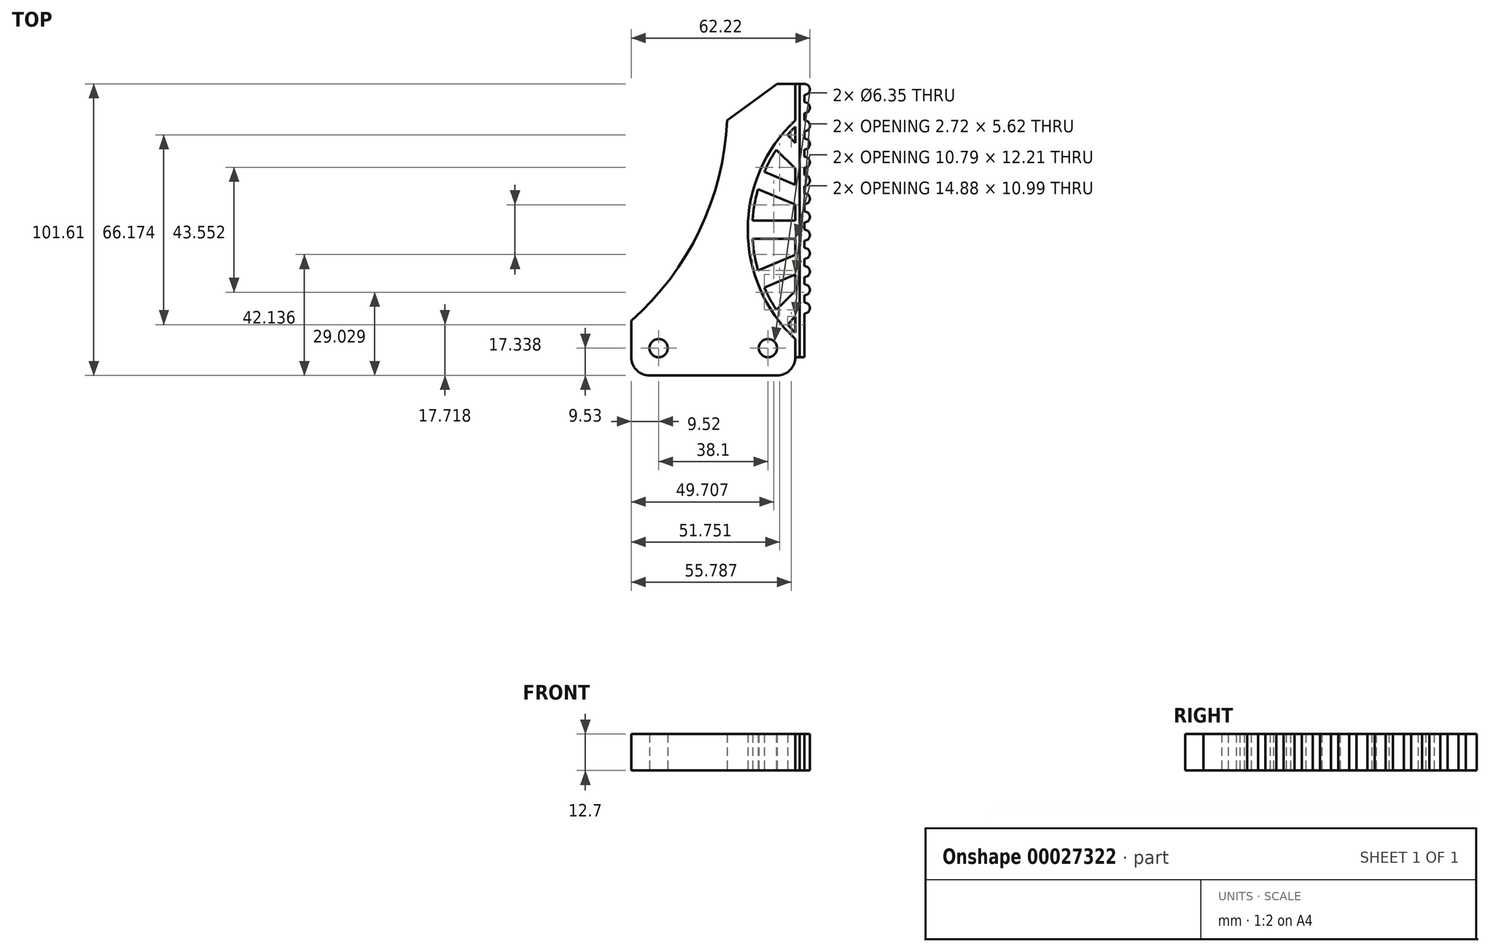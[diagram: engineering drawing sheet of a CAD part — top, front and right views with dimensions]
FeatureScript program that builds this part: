
annotation { "Feature Type Name" : "Feature", "Feature Type Description" : "" }
export const myFeature = defineFeature(function(context is Context, id is Id, definition is map)
    precondition{}
    {
        {
            var Q0;
            Q0=qCreatedBy(makeId("Top.planeOp"),FACE);
            var sketch = newSketch(context, id + "F0", { "sketchPlane" : qUnion([Q0])});
            skCircle(sketch, "E0", {"center": v(0, 0) * mm, "radius": 3.18 * mm});
            skCircle(sketch, "E1", {"center": v(-38.1, 0) * mm, "radius": 3.18 * mm});
            skLineSegment(sketch, "E2", {"start": v(3.18, -9.52) * mm, "end": v(-41.27, -9.53) * mm});
            skLineSegment(sketch, "E3", {"start": v(-47.62, -3.18) * mm, "end": v(-47.62, 9.53) * mm});
            skArc(sketch, "E4", {"start": v(-47.62, 9.52) * mm, "mid": v(-23.82, 41.05) * mm, "end": v(-14.24, 79.38) * mm});
            skLineSegment(sketch, "E5", {"start": v(9.53, -3.17) * mm, "end": v(9.53, 3.18) * mm});
            skArc(sketch, "E6", {"start": v(9.52, 79.37) * mm, "mid": v(-7.04, 41.28) * mm, "end": v(9.52, 3.18) * mm});
            skLineSegment(sketch, "E7", {"start": v(9.53, 79.38) * mm, "end": v(9.53, 92.07) * mm});
            skLineSegment(sketch, "E8", {"start": v(9.52, 92.07) * mm, "end": v(3.17, 92.07) * mm});
            skLineSegment(sketch, "E9", {"start": v(3.18, 92.08) * mm, "end": v(-14.24, 79.38) * mm});
            skPoint(sketch, "E10.visualSharp", {"position": v(9.53, -9.52) * mm});
            skArc(sketch, "E10.filletArc", {"start": v(3.18, -9.52) * mm, "mid": v(7.67, -7.67) * mm, "end": v(9.53, -3.17) * mm});
            skPoint(sketch, "E11.visualSharp", {"position": v(-47.62, -9.53) * mm});
            skArc(sketch, "E11.filletArc", {"start": v(-47.62, -3.18) * mm, "mid": v(-45.77, -7.67) * mm, "end": v(-41.27, -9.53) * mm});
            skLineSegment(sketch, "E12", {"start": v(11.11, 92.07) * mm, "end": v(11.11, -3.17) * mm});
            skArc(sketch, "E13", {"start": v(9.52, 77.17) * mm, "mid": v(-5.45, 41.27) * mm, "end": v(9.52, 5.38) * mm});
            skLineSegment(sketch, "E14", {"start": v(9.53, 77.17) * mm, "end": v(9.53, 71.55) * mm});
            skLineSegment(sketch, "E15", {"start": v(9.53, 71.55) * mm, "end": v(6.8, 74.27) * mm});
            skLineSegment(sketch, "E16", {"start": v(9.53, 62.57) * mm, "end": v(2.94, 69.16) * mm});
            skLineSegment(sketch, "E17", {"start": v(9.53, 62.57) * mm, "end": v(9.53, 56.95) * mm});
            skLineSegment(sketch, "E18", {"start": v(9.52, 38.1) * mm, "end": v(-5.35, 38.1) * mm});
            skLineSegment(sketch, "E19", {"start": v(9.52, 44.45) * mm, "end": v(-5.35, 44.45) * mm});
            skLineSegment(sketch, "E20", {"start": v(9.53, 44.45) * mm, "end": v(9.53, 38.1) * mm, "construction": true});
            skPoint(sketch, "E21", {"position": v(9.52, 41.28) * mm});
            skLineSegment(sketch, "E22", {"start": v(9.53, 56.95) * mm, "end": v(-1.26, 61.42) * mm});
            skLineSegment(sketch, "E23", {"start": v(9.53, 50.07) * mm, "end": v(-3.43, 55.44) * mm});
            skLineSegment(sketch, "E24.trimOffspring", {"start": v(9.53, 50.07) * mm, "end": v(9.53, 44.45) * mm});
            skLineSegment(sketch, "E25", {"start": v(8.17, 72.9) * mm, "end": v(3.68, 68.42) * mm, "construction": true});
            skLineSegment(sketch, "E26", {"start": v(4.13, 59.18) * mm, "end": v(1.7, 53.31) * mm, "construction": true});
            skLineSegment(sketch, "E27", {"start": v(2.09, 44.45) * mm, "end": v(2.09, 38.1) * mm, "construction": true});
            skLineSegment(sketch, "E28", {"start": v(45.06, 41.28) * mm, "end": v(59.1, 41.28) * mm, "construction": true});
            skLineSegment(sketch, "E29.MirrorCS", {"start": v(9.53, 32.48) * mm, "end": v(9.53, 38.1) * mm});
            skLineSegment(sketch, "E30.MirrorCS", {"start": v(9.53, 32.48) * mm, "end": v(-3.43, 27.11) * mm});
            skLineSegment(sketch, "E31.MirrorCS", {"start": v(9.53, 19.98) * mm, "end": v(2.94, 13.4) * mm});
            skLineSegment(sketch, "E32.MirrorCS", {"start": v(9.53, 19.98) * mm, "end": v(9.53, 25.6) * mm});
            skLineSegment(sketch, "E33.MirrorCS", {"start": v(9.53, 25.6) * mm, "end": v(-1.26, 21.13) * mm});
            skLineSegment(sketch, "E34.MirrorCS", {"start": v(9.53, 5.38) * mm, "end": v(9.53, 11) * mm});
            skLineSegment(sketch, "E35.MirrorCS", {"start": v(9.53, 11) * mm, "end": v(6.8, 8.28) * mm});
            skLineSegment(sketch, "E36", {"start": v(11.11, -3.17) * mm, "end": v(9.53, -3.17) * mm});
            skLineSegment(sketch, "E37", {"start": v(11.11, 92.07) * mm, "end": v(9.52, 92.07) * mm});
            skLineSegment(sketch, "E38", {"start": v(11.11, 92.07) * mm, "end": v(12.7, 92.07) * mm});
            skLineSegment(sketch, "E39", {"start": v(12.7, 92.07) * mm, "end": v(12.7, -3.17) * mm});
            skLineSegment(sketch, "E40", {"start": v(12.7, -3.17) * mm, "end": v(11.11, -3.17) * mm});
            skArc(sketch, "E41", {"start": v(12.7, 88.27) * mm, "mid": v(14.6, 90.17) * mm, "end": v(12.7, 92.08) * mm});
            skArc(sketch, "E42.1.0.0", {"start": v(12.7, 81.92) * mm, "mid": v(14.6, 83.82) * mm, "end": v(12.7, 85.73) * mm});
            skArc(sketch, "E42.2.0.0", {"start": v(12.7, 75.57) * mm, "mid": v(14.6, 77.47) * mm, "end": v(12.7, 79.38) * mm});
            skLineSegment(sketch, "E42.direction1", {"start": v(12.7, 88.27) * mm, "end": v(12.7, 81.92) * mm, "construction": true});
            skArc(sketch, "E43.0.3.0", {"start": v(12.7, 69.22) * mm, "mid": v(14.6, 71.12) * mm, "end": v(12.7, 73.03) * mm});
            skArc(sketch, "E43.0.4.0", {"start": v(12.7, 62.87) * mm, "mid": v(14.6, 64.77) * mm, "end": v(12.7, 66.68) * mm});
            skArc(sketch, "E43.0.5.0", {"start": v(12.7, 56.52) * mm, "mid": v(14.6, 58.42) * mm, "end": v(12.7, 60.33) * mm});
            skArc(sketch, "E43.0.6.0", {"start": v(12.7, 50.17) * mm, "mid": v(14.6, 52.07) * mm, "end": v(12.7, 53.98) * mm});
            skArc(sketch, "E43.0.7.0", {"start": v(12.7, 43.82) * mm, "mid": v(14.6, 45.72) * mm, "end": v(12.7, 47.63) * mm});
            skArc(sketch, "E43.0.8.0", {"start": v(12.7, 37.47) * mm, "mid": v(14.6, 39.37) * mm, "end": v(12.7, 41.28) * mm});
            skArc(sketch, "E43.0.9.0", {"start": v(12.7, 31.12) * mm, "mid": v(14.6, 33.02) * mm, "end": v(12.7, 34.93) * mm});
            skArc(sketch, "E43.0.10.0", {"start": v(12.7, 24.77) * mm, "mid": v(14.6, 26.67) * mm, "end": v(12.7, 28.58) * mm});
            skArc(sketch, "E43.0.11.0", {"start": v(12.7, 18.42) * mm, "mid": v(14.6, 20.32) * mm, "end": v(12.7, 22.23) * mm});
            skArc(sketch, "E43.0.12.0", {"start": v(12.7, 12.07) * mm, "mid": v(14.6, 13.97) * mm, "end": v(12.7, 15.88) * mm});
            skArc(sketch, "E44.0.13.0", {"start": v(12.7, 5.72) * mm, "mid": v(14.6, 7.62) * mm, "end": v(12.7, 9.53) * mm});
            skArc(sketch, "E44.0.14.0", {"start": v(12.7, -0.63) * mm, "mid": v(14.6, 1.27) * mm, "end": v(12.7, 3.18) * mm});
            skSolve(sketch);
        }
        {
            var Q0;
            Q0=makeQuery(id+"F0.imprint","IMPRINT",FACE,{"disambiguationData":[TD([[makeQuery(id+"F0.imprint","IMPRINT",EDGE,{"derivedFrom":sQuery(id+"F0.wireOp",EDGE,"E0")}),-1.0]])]});
            extrude(context, id + "F1", {"entities" : qUnion([Q0]), "depth" : 12.7 * mm});
        }
        {
            var Q0;
            Q0=makeQuery(id+"F0.imprint","IMPRINT",FACE,{"disambiguationData":[TD([[makeQuery(id+"F0.imprint","IMPRINT",EDGE,{"derivedFrom":sQuery(id+"F0.wireOp",EDGE,"E5")}),-1.0]])]});
            extrude(context, id + "F2", {"entities" : qUnion([Q0]), "depth" : 12.7 * mm});
        }
        {
            var Q0;
            Q0=makeQuery(id+"F0.imprint","IMPRINT",FACE,{"disambiguationData":[TD([[makeQuery(id+"F0.imprint","IMPRINT",EDGE,{"derivedFrom":sQuery(id+"F0.wireOp",EDGE,"E12")}),1.0]])]});
            var Q1;
            {var subQ0=sQuery(id+"F0.wireOp",EDGE,"E41");Q1=makeQuery(id+"F0.imprint","IMPRINT",FACE,{"disambiguationData":[TD([[makeQuery(id+"F0.imprint","IMPRINT",EDGE,{"derivedFrom":subQ0}),1.0]])]});}
            var Q2;
            {var subQ0=sQuery(id+"F0.wireOp",EDGE,"E42.1.0.0");Q2=makeQuery(id+"F0.imprint","IMPRINT",FACE,{"disambiguationData":[TD([[makeQuery(id+"F0.imprint","IMPRINT",EDGE,{"derivedFrom":subQ0}),1.0]])]});}
            var Q3;
            {var subQ0=sQuery(id+"F0.wireOp",EDGE,"E42.2.0.0");Q3=makeQuery(id+"F0.imprint","IMPRINT",FACE,{"disambiguationData":[TD([[makeQuery(id+"F0.imprint","IMPRINT",EDGE,{"derivedFrom":subQ0}),1.0]])]});}
            var Q4;
            {var subQ0=sQuery(id+"F0.wireOp",EDGE,"E43.0.10.0");Q4=makeQuery(id+"F0.imprint","IMPRINT",FACE,{"disambiguationData":[TD([[makeQuery(id+"F0.imprint","IMPRINT",EDGE,{"derivedFrom":subQ0}),1.0]])]});}
            var Q5;
            {var subQ0=sQuery(id+"F0.wireOp",EDGE,"E43.0.7.0");Q5=makeQuery(id+"F0.imprint","IMPRINT",FACE,{"disambiguationData":[TD([[makeQuery(id+"F0.imprint","IMPRINT",EDGE,{"derivedFrom":subQ0}),1.0]])]});}
            var Q6;
            {var subQ0=sQuery(id+"F0.wireOp",EDGE,"E43.0.5.0");Q6=makeQuery(id+"F0.imprint","IMPRINT",FACE,{"disambiguationData":[TD([[makeQuery(id+"F0.imprint","IMPRINT",EDGE,{"derivedFrom":subQ0}),1.0]])]});}
            var Q7;
            {var subQ0=sQuery(id+"F0.wireOp",EDGE,"E43.0.3.0");Q7=makeQuery(id+"F0.imprint","IMPRINT",FACE,{"disambiguationData":[TD([[makeQuery(id+"F0.imprint","IMPRINT",EDGE,{"derivedFrom":subQ0}),1.0]])]});}
            var Q8;
            {var subQ0=sQuery(id+"F0.wireOp",EDGE,"E43.0.4.0");Q8=makeQuery(id+"F0.imprint","IMPRINT",FACE,{"disambiguationData":[TD([[makeQuery(id+"F0.imprint","IMPRINT",EDGE,{"derivedFrom":subQ0}),1.0]])]});}
            var Q9;
            {var subQ0=sQuery(id+"F0.wireOp",EDGE,"E43.0.6.0");Q9=makeQuery(id+"F0.imprint","IMPRINT",FACE,{"disambiguationData":[TD([[makeQuery(id+"F0.imprint","IMPRINT",EDGE,{"derivedFrom":subQ0}),1.0]])]});}
            var Q10;
            {var subQ0=sQuery(id+"F0.wireOp",EDGE,"E43.0.9.0");Q10=makeQuery(id+"F0.imprint","IMPRINT",FACE,{"disambiguationData":[TD([[makeQuery(id+"F0.imprint","IMPRINT",EDGE,{"derivedFrom":subQ0}),1.0]])]});}
            var Q11;
            {var subQ0=sQuery(id+"F0.wireOp",EDGE,"E43.0.8.0");Q11=makeQuery(id+"F0.imprint","IMPRINT",FACE,{"disambiguationData":[TD([[makeQuery(id+"F0.imprint","IMPRINT",EDGE,{"derivedFrom":subQ0}),1.0]])]});}
            var Q12;
            {var subQ0=sQuery(id+"F0.wireOp",EDGE,"E43.0.11.0");Q12=makeQuery(id+"F0.imprint","IMPRINT",FACE,{"disambiguationData":[TD([[makeQuery(id+"F0.imprint","IMPRINT",EDGE,{"derivedFrom":subQ0}),1.0]])]});}
            var Q13;
            {var subQ0=sQuery(id+"F0.wireOp",EDGE,"E43.0.12.0");Q13=makeQuery(id+"F0.imprint","IMPRINT",FACE,{"disambiguationData":[TD([[makeQuery(id+"F0.imprint","IMPRINT",EDGE,{"derivedFrom":subQ0}),1.0]])]});}
            extrude(context, id + "F3", {"entities" : qUnion([Q0, Q1, Q2, Q3, Q4, Q5, Q6, Q7, Q8, Q9, Q10, Q11, Q12, Q13]), "depth" : 12.7 * mm});
        }
    });
